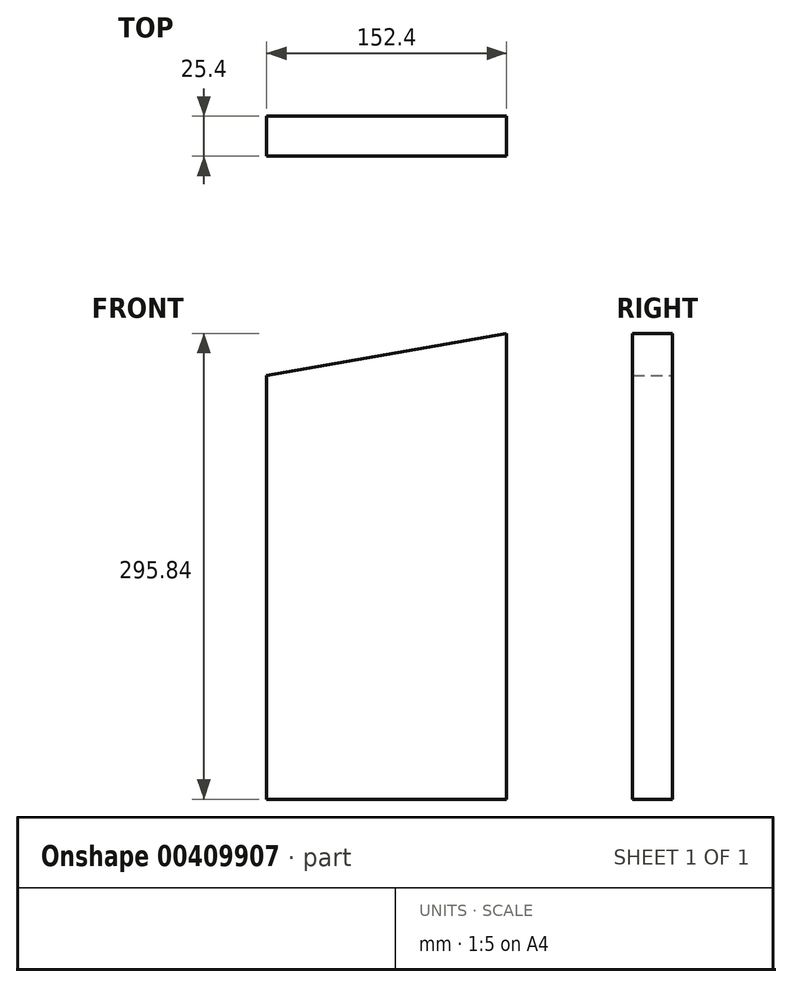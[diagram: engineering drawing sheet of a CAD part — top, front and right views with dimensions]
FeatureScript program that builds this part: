
annotation { "Feature Type Name" : "Feature", "Feature Type Description" : "" }
export const myFeature = defineFeature(function(context is Context, id is Id, definition is map)
    precondition{}
    {
        {
            var Q0;
            Q0=qCreatedBy(makeId("Front.planeOp"),FACE);
            var sketch = newSketch(context, id + "F0", { "sketchPlane" : qUnion([Q0])});
            skLineSegment(sketch, "E0.bottom", {"start": v(-105.55, 148) * mm, "end": v(46.85, 148) * mm});
            skLineSegment(sketch, "E0.top", {"start": v(-105.55, -156.8) * mm, "end": v(46.85, -156.8) * mm});
            skLineSegment(sketch, "E0.left", {"start": v(-105.55, 148) * mm, "end": v(-105.55, -156.8) * mm});
            skLineSegment(sketch, "E0.right", {"start": v(46.85, 148) * mm, "end": v(46.85, -156.8) * mm});
            skSolve(sketch);
        }
        {
            var Q0;
            Q0=qSketchRegion(id+"F0",true);
            extrude(context, id + "F1", {"entities" : qUnion([Q0]), "depth" : 25.4 * mm});
        }
        {
            var Q0;
            Q0=makeQuery(id+"F1.opExtrude","SWEPT_EDGE",EDGE,{"disambiguationData":[OSD([sQuery(id+"F0.wireOp",EDGE,"E0.bottom"),sQuery(id+"F0.wireOp",EDGE,"E0.left")])]});
            chamfer(context, id + "F2", {"entities" : qUnion([Q0]), "chamferType" : ChamferType.OFFSET_ANGLE, "width" : 203.2 * mm, "oppositeDirection" : true, "angle" : 10 * degree, "tangentPropagation" : true});
        }
    });
